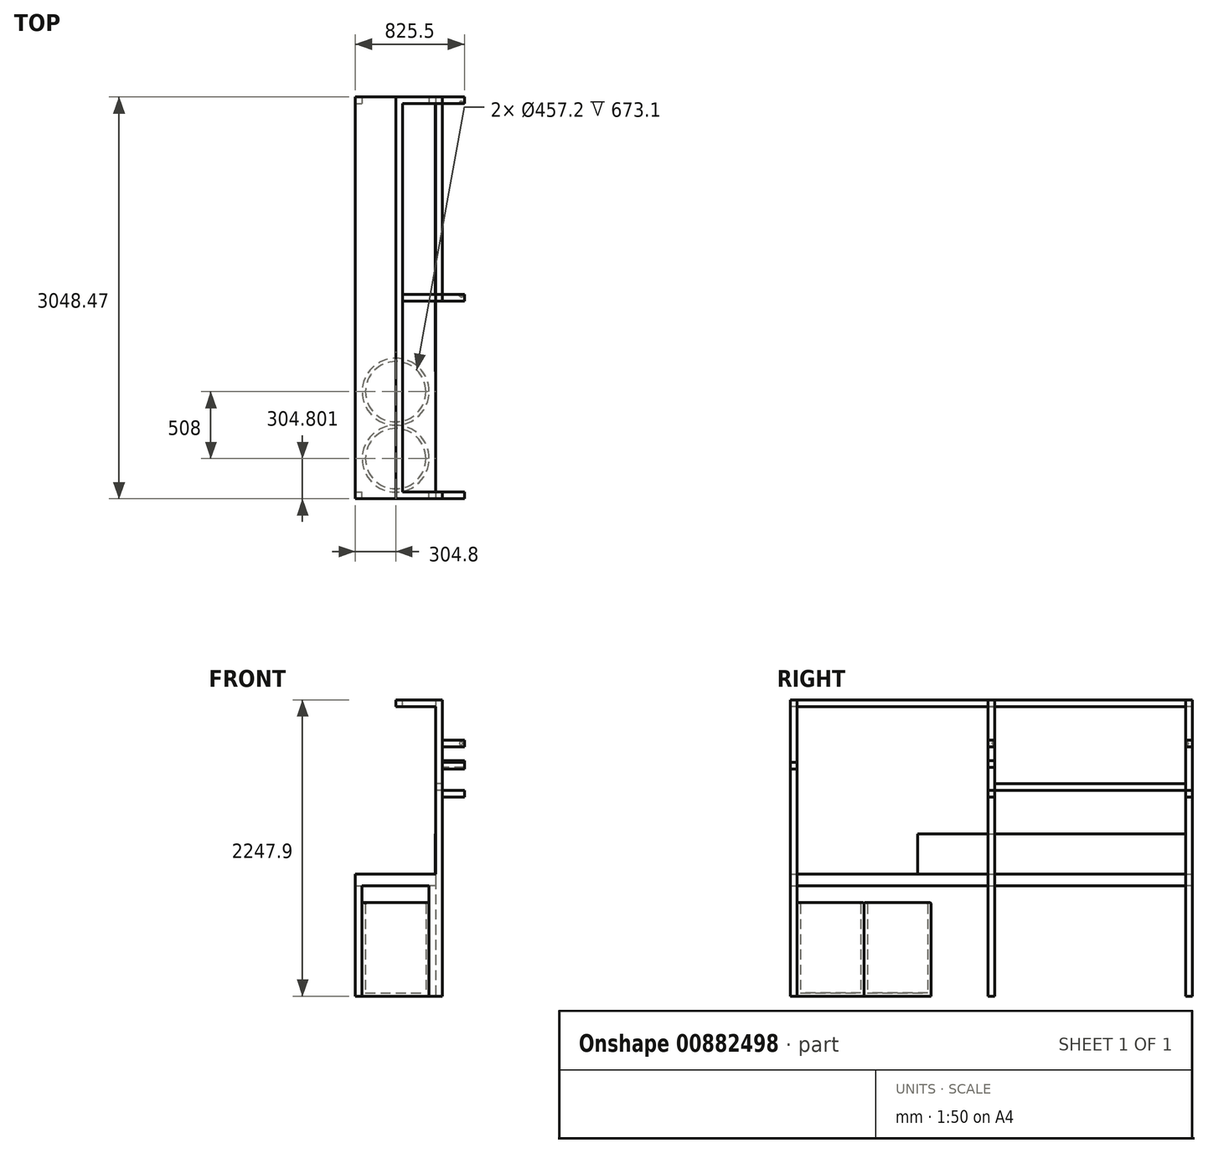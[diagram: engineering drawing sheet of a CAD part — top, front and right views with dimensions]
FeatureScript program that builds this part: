
annotation { "Feature Type Name" : "Feature", "Feature Type Description" : "" }
export const myFeature = defineFeature(function(context is Context, id is Id, definition is map)
    precondition{}
    {
        {
            var Q0;
            Q0=qCreatedBy(makeId("Right.planeOp"),FACE);
            var sketch = newSketch(context, id + "F0", { "sketchPlane" : qUnion([Q0])});
            skLineSegment(sketch, "E0.bottom", {"start": v(-1340.3, -28.95) * mm, "end": v(1707.7, -28.95) * mm});
            skLineSegment(sketch, "E0.top", {"start": v(-1340.3, -117.85) * mm, "end": v(1707.7, -117.85) * mm});
            skLineSegment(sketch, "E0.left", {"start": v(-1340.3, -28.95) * mm, "end": v(-1340.3, -117.85) * mm});
            skLineSegment(sketch, "E0.right", {"start": v(1707.7, -28.95) * mm, "end": v(1707.7, -117.85) * mm});
            skSolve(sketch);
        }
        {
            var Q0;
            Q0=makeQuery(id+"F0.imprint","IMPRINT",FACE,{"disambiguationData":[TD([[makeQuery(id+"F0.imprint","IMPRINT",EDGE,{"derivedFrom":sQuery(id+"F0.wireOp",EDGE,"E0.bottom")}),-1.0]])]});
            extrude(context, id + "F1", {"entities" : qUnion([Q0]), "oppositeDirection" : true, "depth" : 609.6 * mm, "offsetDistance" : 25.4 * mm});
        }
        {
            var Q0;
            Q0=makeQuery(id+"F1.opExtrude","SWEPT_FACE",FACE,{"disambiguationData":[OSD([sQuery(id+"F0.wireOp",EDGE,"E0.top")])]});
            var sketch = newSketch(context, id + "F2", { "sketchPlane" : qUnion([Q0])});
            skLineSegment(sketch, "E1.bottom", {"start": v(-609.6, 1340.3) * mm, "end": v(-558.8, 1340.3) * mm});
            skLineSegment(sketch, "E1.top", {"start": v(-609.6, 1289.5) * mm, "end": v(-558.8, 1289.5) * mm});
            skLineSegment(sketch, "E1.left", {"start": v(-609.6, 1340.3) * mm, "end": v(-609.6, 1289.5) * mm});
            skLineSegment(sketch, "E1.right", {"start": v(-558.8, 1340.3) * mm, "end": v(-558.8, 1289.5) * mm});
            skLineSegment(sketch, "E2.bottom", {"start": v(0, 1340.3) * mm, "end": v(-50.8, 1340.3) * mm});
            skLineSegment(sketch, "E2.top", {"start": v(0, 1289.5) * mm, "end": v(-50.8, 1289.5) * mm});
            skLineSegment(sketch, "E2.left", {"start": v(0, 1340.3) * mm, "end": v(0, 1289.5) * mm});
            skLineSegment(sketch, "E2.right", {"start": v(-50.8, 1340.3) * mm, "end": v(-50.8, 1289.5) * mm});
            skLineSegment(sketch, "E3.bottom", {"start": v(0, -1707.7) * mm, "end": v(-50.8, -1707.7) * mm});
            skLineSegment(sketch, "E3.top", {"start": v(0, -1656.9) * mm, "end": v(-50.8, -1656.9) * mm});
            skLineSegment(sketch, "E3.left", {"start": v(0, -1707.7) * mm, "end": v(0, -1656.9) * mm});
            skLineSegment(sketch, "E3.right", {"start": v(-50.8, -1707.7) * mm, "end": v(-50.8, -1656.9) * mm});
            skLineSegment(sketch, "E4.bottom", {"start": v(-609.6, -1707.7) * mm, "end": v(-558.8, -1707.7) * mm});
            skLineSegment(sketch, "E4.top", {"start": v(-609.6, -1656.9) * mm, "end": v(-558.8, -1656.9) * mm});
            skLineSegment(sketch, "E4.left", {"start": v(-609.6, -1707.7) * mm, "end": v(-609.6, -1656.9) * mm});
            skLineSegment(sketch, "E4.right", {"start": v(-558.8, -1707.7) * mm, "end": v(-558.8, -1656.9) * mm});
            skSolve(sketch);
        }
        {
            var Q0;
            Q0=qSketchRegion(id+"F2",true);
            extrude(context, id + "F3", {"entities" : qUnion([Q0]), "operationType" : NewBodyOperationType.ADD, "depth" : 838.2 * mm, "offsetDistance" : 25.4 * mm});
        }
        {
            var Q0;
            Q0=makeQuery(id+"F3.opExtrude","CAP_FACE",FACE,{"disambiguationData":[OSD([sQuery(id+"F2.wireOp",EDGE,"E4.bottom"),sQuery(id+"F2.wireOp",EDGE,"E4.top"),sQuery(id+"F2.wireOp",EDGE,"E4.left"),sQuery(id+"F2.wireOp",EDGE,"E4.right")])],"isStart":false});
            var sketch = newSketch(context, id + "F4", { "sketchPlane" : qUnion([Q0])});
            skCircle(sketch, "E5", {"center": v(-304.8, 1035.5) * mm, "radius": 254 * mm});
            skCircle(sketch, "E6", {"center": v(-304.8, 527.5) * mm, "radius": 254 * mm});
            skSolve(sketch);
        }
        {
            var Q0;
            Q0=qSketchRegion(id+"F4",true);
            extrude(context, id + "F5", {"entities" : qUnion([Q0]), "oppositeDirection" : true, "depth" : 711.2 * mm, "offsetDistance" : 25.4 * mm});
        }
        {
            var Q0;
            Q0=makeQuery(id+"F3.opExtrude","CAP_FACE",FACE,{"disambiguationData":[OSD([sQuery(id+"F2.wireOp",EDGE,"E2.bottom"),sQuery(id+"F2.wireOp",EDGE,"E2.top"),sQuery(id+"F2.wireOp",EDGE,"E2.left"),sQuery(id+"F2.wireOp",EDGE,"E2.right")])],"isStart":false});
            var sketch = newSketch(context, id + "F6", { "sketchPlane" : qUnion([Q0])});
            skLineSegment(sketch, "E7.bottom", {"start": v(0, 1340.3) * mm, "end": v(50.8, 1340.3) * mm});
            skLineSegment(sketch, "E7.top", {"start": v(0, 1289.5) * mm, "end": v(50.8, 1289.5) * mm});
            skLineSegment(sketch, "E7.left", {"start": v(0, 1340.3) * mm, "end": v(0, 1289.5) * mm});
            skLineSegment(sketch, "E7.right", {"start": v(50.8, 1340.3) * mm, "end": v(50.8, 1289.5) * mm});
            skLineSegment(sketch, "E8.bottom", {"start": v(0, -1656.9) * mm, "end": v(50.8, -1656.9) * mm});
            skLineSegment(sketch, "E8.top", {"start": v(0, -1707.7) * mm, "end": v(50.8, -1707.7) * mm});
            skLineSegment(sketch, "E8.left", {"start": v(0, -1656.9) * mm, "end": v(0, -1707.7) * mm});
            skLineSegment(sketch, "E8.right", {"start": v(50.8, -1656.9) * mm, "end": v(50.8, -1707.7) * mm});
            skSolve(sketch);
        }
        {
            var Q0;
            Q0=qSketchRegion(id+"F6",true);
            extrude(context, id + "F7", {"entities" : qUnion([Q0]), "operationType" : NewBodyOperationType.ADD, "oppositeDirection" : true, "depth" : 2247.9 * mm, "offsetDistance" : 25.4 * mm});
        }
        {
            var Q0;
            Q0=makeQuery(id+"F7.opExtrude","SWEPT_FACE",FACE,{"disambiguationData":[OSD([sQuery(id+"F6.wireOp",EDGE,"E8.left")])]});
            var sketch = newSketch(context, id + "F8", { "sketchPlane" : qUnion([Q0])});
            skLineSegment(sketch, "E9.bottom", {"start": v(-1707.7, 1291.85) * mm, "end": v(1340.3, 1291.85) * mm});
            skLineSegment(sketch, "E9.top", {"start": v(-1707.7, 1241.05) * mm, "end": v(1340.3, 1241.05) * mm});
            skLineSegment(sketch, "E9.left", {"start": v(-1707.7, 1291.85) * mm, "end": v(-1707.7, 1241.05) * mm});
            skLineSegment(sketch, "E9.right", {"start": v(1340.3, 1291.85) * mm, "end": v(1340.3, 1241.05) * mm});
            skSolve(sketch);
        }
        {
            var Q0;
            Q0=qSketchRegion(id+"F8",true);
            extrude(context, id + "F9", {"entities" : qUnion([Q0]), "operationType" : NewBodyOperationType.ADD, "depth" : 304.8 * mm, "offsetDistance" : 25.4 * mm});
        }
        {
            var Q0;
            Q0=makeQuery(id+"F9.boolean.opBoolean","MERGE",FACE,{"derivedFrom":[makeQuery(id+"F7.opExtrude","CAP_FACE",FACE,{"disambiguationData":[OSD([sQuery(id+"F6.wireOp",EDGE,"E7.bottom"),sQuery(id+"F6.wireOp",EDGE,"E7.top"),sQuery(id+"F6.wireOp",EDGE,"E7.left"),sQuery(id+"F6.wireOp",EDGE,"E7.right")])],"isStart":false}),makeQuery(id+"F7.opExtrude","CAP_FACE",FACE,{"disambiguationData":[OSD([sQuery(id+"F6.wireOp",EDGE,"E8.bottom"),sQuery(id+"F6.wireOp",EDGE,"E8.top"),sQuery(id+"F6.wireOp",EDGE,"E8.left"),sQuery(id+"F6.wireOp",EDGE,"E8.right")])],"isStart":false}),makeQuery(id+"F9.opExtrude","SWEPT_FACE",FACE,{"disambiguationData":[OSD([sQuery(id+"F8.wireOp",EDGE,"E9.bottom")])]})]});
            var sketch = newSketch(context, id + "F10", { "sketchPlane" : qUnion([Q0])});
            skLineSegment(sketch, "E10.bottom", {"start": v(0, 1656.9) * mm, "end": v(-254, 1656.9) * mm});
            skLineSegment(sketch, "E10.top", {"start": v(0, -1289.5) * mm, "end": v(-254, -1289.5) * mm});
            skLineSegment(sketch, "E10.left", {"start": v(0, 1656.9) * mm, "end": v(0, -1289.5) * mm});
            skLineSegment(sketch, "E10.right", {"start": v(-254, 1656.9) * mm, "end": v(-254, -1289.5) * mm});
            skSolve(sketch);
        }
        {
            var Q0;
            Q0=qSketchRegion(id+"F10",true);
            extrude(context, id + "F11", {"entities" : qUnion([Q0]), "operationType" : NewBodyOperationType.REMOVE, "endBound" : BoundingType.UP_TO_NEXT, "oppositeDirection" : true, "depth" : 25.4 * mm, "offsetDistance" : 25.4 * mm});
        }
        {
            var Q0;
            Q0=makeQuery(id+"F1.opExtrude","SWEPT_FACE",FACE,{"disambiguationData":[OSD([sQuery(id+"F0.wireOp",EDGE,"E0.bottom")])]});
            var sketch = newSketch(context, id + "F12", { "sketchPlane" : qUnion([Q0])});
            skLineSegment(sketch, "E11.bottom", {"start": v(0, 1656.9) * mm, "end": v(-3.17, 1656.9) * mm});
            skLineSegment(sketch, "E11.top", {"start": v(0, -375.1) * mm, "end": v(-3.17, -375.1) * mm});
            skLineSegment(sketch, "E11.left", {"start": v(0, 1656.9) * mm, "end": v(0, -375.1) * mm});
            skLineSegment(sketch, "E11.right", {"start": v(-3.18, 1656.9) * mm, "end": v(-3.17, -375.1) * mm});
            skSolve(sketch);
        }
        {
            var Q0;
            Q0=qSketchRegion(id+"F12",true);
            extrude(context, id + "F13", {"entities" : qUnion([Q0]), "depth" : 304.8 * mm, "offsetDistance" : 25.4 * mm});
        }
        {
            var Q0;
            Q0=makeQuery(id+"F7.boolean.opBoolean","MERGE",FACE,{"derivedFrom":[makeQuery(id+"F3.opExtrude","CAP_FACE",FACE,{"disambiguationData":[OSD([sQuery(id+"F2.wireOp",EDGE,"E2.bottom"),sQuery(id+"F2.wireOp",EDGE,"E2.top"),sQuery(id+"F2.wireOp",EDGE,"E2.left"),sQuery(id+"F2.wireOp",EDGE,"E2.right")])],"isStart":false}),makeQuery(id+"F7.opExtrude","CAP_FACE",FACE,{"disambiguationData":[OSD([sQuery(id+"F6.wireOp",EDGE,"E7.bottom"),sQuery(id+"F6.wireOp",EDGE,"E7.top"),sQuery(id+"F6.wireOp",EDGE,"E7.left"),sQuery(id+"F6.wireOp",EDGE,"E7.right")])],"isStart":true})]});
            var sketch = newSketch(context, id + "F14", { "sketchPlane" : qUnion([Q0])});
            skLineSegment(sketch, "E12.bottom", {"start": v(0, -158.3) * mm, "end": v(50.8, -158.3) * mm});
            skLineSegment(sketch, "E12.top", {"start": v(0, -209.1) * mm, "end": v(50.8, -209.1) * mm});
            skLineSegment(sketch, "E12.left", {"start": v(0, -158.3) * mm, "end": v(0, -209.1) * mm});
            skLineSegment(sketch, "E12.right", {"start": v(50.8, -158.3) * mm, "end": v(50.8, -209.1) * mm});
            skSolve(sketch);
        }
        {
            var Q0;
            Q0=qSketchRegion(id+"F14",true);
            extrude(context, id + "F15", {"entities" : qUnion([Q0]), "oppositeDirection" : true, "depth" : 2247.9 * mm, "offsetDistance" : 25.4 * mm});
        }
        {
            var Q0;
            Q0=makeQuery(id+"F5.opExtrude","CAP_FACE",FACE,{"disambiguationData":[OSD([sQuery(id+"F4.wireOp",EDGE,"E6")])],"isStart":false});
            shell(context, id + "F16", {"entities" : qUnion([Q0]), "thickness" : 25.4 * mm});
        }
        {
            var Q0;
            Q0=makeQuery(id+"F5.opExtrude","CAP_FACE",FACE,{"disambiguationData":[OSD([sQuery(id+"F4.wireOp",EDGE,"E5")])],"isStart":false});
            shell(context, id + "F17", {"entities" : qUnion([Q0]), "thickness" : 25.4 * mm});
        }
        {
            var Q0;
            Q0=makeQuery(id+"F5.opExtrude","CAP_FACE",FACE,{"disambiguationData":[OSD([sQuery(id+"F4.wireOp",EDGE,"E5")])],"isStart":false});
            fillet(context, id + "F18", {"entities" : qUnion([Q0]), "radius" : 12.7 * mm, "tangentPropagation" : true, "allowEdgeOverflow" : false});
        }
        {
            var Q0;
            Q0=makeQuery(id+"F5.opExtrude","CAP_FACE",FACE,{"disambiguationData":[OSD([sQuery(id+"F4.wireOp",EDGE,"E6")])],"isStart":false});
            fillet(context, id + "F19", {"entities" : qUnion([Q0]), "radius" : 12.7 * mm, "tangentPropagation" : true, "allowEdgeOverflow" : false});
        }
        {
            var Q0;
            Q0=makeQuery(id+"F11.boolean.opBoolean","MERGE",FACE,{"derivedFrom":[makeQuery(id+"F7.boolean.opBoolean","MERGE",FACE,{"derivedFrom":[makeQuery(id+"F3.opExtrude","SWEPT_FACE",FACE,{"disambiguationData":[OSD([sQuery(id+"F2.wireOp",EDGE,"E3.top")])]}),makeQuery(id+"F7.opExtrude","SWEPT_FACE",FACE,{"disambiguationData":[OSD([sQuery(id+"F6.wireOp",EDGE,"E8.bottom")])]})]})],"fromTools":[makeQuery(id+"F11.opExtrude","SWEPT_FACE",FACE,{"disambiguationData":[OSD([sQuery(id+"F10.wireOp",EDGE,"E10.bottom")])]})]});
            var sketch = newSketch(context, id + "F20", { "sketchPlane" : qUnion([Q0])});
            skLineSegment(sketch, "E13.bottom", {"start": v(0, 656.85) * mm, "end": v(50.8, 656.85) * mm});
            skLineSegment(sketch, "E13.top", {"start": v(0, 606.05) * mm, "end": v(50.8, 606.05) * mm});
            skLineSegment(sketch, "E13.left", {"start": v(0, 656.85) * mm, "end": v(0, 606.05) * mm});
            skLineSegment(sketch, "E13.right", {"start": v(50.8, 656.85) * mm, "end": v(50.8, 606.05) * mm});
            skSolve(sketch);
        }
        {
            var Q0;
            Q0=qSketchRegion(id+"F20",true);
            extrude(context, id + "F21", {"entities" : qUnion([Q0]), "endBound" : BoundingType.UP_TO_NEXT, "depth" : 25.4 * mm, "offsetDistance" : 25.4 * mm});
        }
        {
            var Q0;
            Q0=makeQuery(id+"F15.opExtrude","SWEPT_FACE",FACE,{"disambiguationData":[OSD([sQuery(id+"F14.wireOp",EDGE,"E12.right")])]});
            var sketch = newSketch(context, id + "F22", { "sketchPlane" : qUnion([Q0])});
            skLineSegment(sketch, "E14.bottom", {"start": v(158.3, 831.1) * mm, "end": v(209.1, 831.1) * mm});
            skLineSegment(sketch, "E14.top", {"start": v(158.3, 780.3) * mm, "end": v(209.1, 780.3) * mm});
            skLineSegment(sketch, "E14.left", {"start": v(158.3, 831.1) * mm, "end": v(158.3, 780.3) * mm});
            skLineSegment(sketch, "E14.right", {"start": v(209.1, 831.1) * mm, "end": v(209.1, 780.3) * mm});
            skLineSegment(sketch, "E15.bottom", {"start": v(-1340.3, 818.75) * mm, "end": v(-1289.5, 818.75) * mm});
            skLineSegment(sketch, "E15.top", {"start": v(-1340.3, 767.95) * mm, "end": v(-1289.5, 767.95) * mm});
            skLineSegment(sketch, "E15.left", {"start": v(-1340.3, 818.75) * mm, "end": v(-1340.3, 767.95) * mm});
            skLineSegment(sketch, "E15.right", {"start": v(-1289.5, 818.75) * mm, "end": v(-1289.5, 767.95) * mm});
            skSolve(sketch);
        }
        {
            var Q0;
            Q0=qSketchRegion(id+"F22",true);
            extrude(context, id + "F23", {"entities" : qUnion([Q0]), "depth" : 165.1 * mm, "offsetDistance" : 25.4 * mm});
        }
        {
            var Q0;
            Q0=makeQuery(id+"F15.opExtrude","SWEPT_FACE",FACE,{"disambiguationData":[OSD([sQuery(id+"F14.wireOp",EDGE,"E12.left")])]});
            var sketch = newSketch(context, id + "F24", { "sketchPlane" : qUnion([Q0])});
            skLineSegment(sketch, "E16.bottom", {"start": v(-209.1, 1291.85) * mm, "end": v(-158.3, 1291.85) * mm});
            skLineSegment(sketch, "E16.top", {"start": v(-209.1, 1241.05) * mm, "end": v(-158.3, 1241.05) * mm});
            skLineSegment(sketch, "E16.left", {"start": v(-209.1, 1291.85) * mm, "end": v(-209.1, 1241.05) * mm});
            skLineSegment(sketch, "E16.right", {"start": v(-158.3, 1291.85) * mm, "end": v(-158.3, 1241.05) * mm});
            skSolve(sketch);
        }
        {
            var Q0;
            Q0=qSketchRegion(id+"F24",true);
            extrude(context, id + "F25", {"entities" : qUnion([Q0]), "endBound" : BoundingType.UP_TO_NEXT, "depth" : 25.4 * mm, "offsetDistance" : 25.4 * mm});
        }
        {
            var Q0;
            Q0=makeQuery(id+"F15.opExtrude","SWEPT_FACE",FACE,{"disambiguationData":[OSD([sQuery(id+"F14.wireOp",EDGE,"E12.right")])]});
            var sketch = newSketch(context, id + "F26", { "sketchPlane" : qUnion([Q0])});
            skLineSegment(sketch, "E17.bottom", {"start": v(209.1, 606.05) * mm, "end": v(158.3, 606.05) * mm});
            skLineSegment(sketch, "E17.top", {"start": v(209.1, 555.25) * mm, "end": v(158.3, 555.25) * mm});
            skLineSegment(sketch, "E17.left", {"start": v(209.1, 606.05) * mm, "end": v(209.1, 555.25) * mm});
            skLineSegment(sketch, "E17.right", {"start": v(158.3, 606.05) * mm, "end": v(158.3, 555.25) * mm});
            skLineSegment(sketch, "E18.bottom", {"start": v(1657.36, 606.05) * mm, "end": v(1708.16, 606.05) * mm});
            skLineSegment(sketch, "E18.top", {"start": v(1657.36, 555.25) * mm, "end": v(1708.16, 555.25) * mm});
            skLineSegment(sketch, "E18.left", {"start": v(1657.36, 606.05) * mm, "end": v(1657.36, 555.25) * mm});
            skLineSegment(sketch, "E18.right", {"start": v(1708.16, 606.05) * mm, "end": v(1708.16, 555.25) * mm});
            skSolve(sketch);
        }
        {
            var Q0;
            Q0 = qSketchRegion(id + "F26", true);
            extrude(context, id + "F27", {"entities" : qUnion([Q0]), "depth" : 165.1 * mm, "offsetDistance" : 25.4 * mm});
        }
        {
            var Q0;
            Q0=makeQuery(id+"F15.opExtrude","SWEPT_FACE",FACE,{"disambiguationData":[OSD([sQuery(id+"F14.wireOp",EDGE,"E12.right")])]});
            var sketch = newSketch(context, id + "F28", { "sketchPlane" : qUnion([Q0])});
            skLineSegment(sketch, "E19.bottom", {"start": v(158.3, 987.05) * mm, "end": v(209.1, 987.05) * mm});
            skLineSegment(sketch, "E19.top", {"start": v(158.3, 936.25) * mm, "end": v(209.1, 936.25) * mm});
            skLineSegment(sketch, "E19.left", {"start": v(158.3, 987.05) * mm, "end": v(158.3, 936.25) * mm});
            skLineSegment(sketch, "E19.right", {"start": v(209.1, 987.05) * mm, "end": v(209.1, 936.25) * mm});
            skLineSegment(sketch, "E20.bottom", {"start": v(1656.9, 987.05) * mm, "end": v(1707.7, 987.05) * mm});
            skLineSegment(sketch, "E20.top", {"start": v(1656.9, 936.25) * mm, "end": v(1707.7, 936.25) * mm});
            skLineSegment(sketch, "E20.left", {"start": v(1656.9, 987.05) * mm, "end": v(1656.9, 936.25) * mm});
            skLineSegment(sketch, "E20.right", {"start": v(1707.7, 987.05) * mm, "end": v(1707.7, 936.25) * mm});
            skSolve(sketch);
        }
        {
            var Q0;
            Q0 = qSketchRegion(id + "F28", true);
            extrude(context, id + "F29", {"entities" : qUnion([Q0]), "depth" : 165.1 * mm, "offsetDistance" : 25.4 * mm});
        }
        {
            var Q0;
            Q0=makeQuery(id+"F29.opExtrude","SWEPT_FACE",FACE,{"disambiguationData":[OSD([sQuery(id+"F28.wireOp",EDGE,"E20.left")])]});
            var sketch = newSketch(context, id + "F30", { "sketchPlane" : qUnion([Q0])});
            skPoint(sketch, "E21", {"position": v(190.5, 961.65) * mm});
            skSolve(sketch);
        }
        {
            var Q0;
            Q0=sQuery(id+"F30.wireOp",VERTEX,"E21");
            var Q1;
            Q1=makeQuery(id+"F29.opExtrude","SWEPT_BODY",BODY,{"disambiguationData":[OSD([sQuery(id+"F28.wireOp",EDGE,"E20.bottom"),sQuery(id+"F28.wireOp",EDGE,"E20.top"),sQuery(id+"F28.wireOp",EDGE,"E20.left"),sQuery(id+"F28.wireOp",EDGE,"E20.right")])]});
            hole(context, id + "F31", {"style" : HoleStyle.SIMPLE, "endStyle" : HoleEndStyle.BLIND, "holeDiameter" : 25.4 * mm, "majorDiameter" : 6.35 * mm, "holeDepth" : 12.7 * mm, "isTappedThrough" : true, "tappedDepth" : 12.7 * mm, "tapClearance" : 3, "locations" : qUnion([Q0]), "scope" : qUnion([Q1])});
        }
        {
            var Q0;
            Q0=makeQuery(id+"F29.opExtrude","SWEPT_FACE",FACE,{"disambiguationData":[OSD([sQuery(id+"F28.wireOp",EDGE,"E19.right")])]});
            var sketch = newSketch(context, id + "F32", { "sketchPlane" : qUnion([Q0])});
            skPoint(sketch, "E22", {"position": v(-190.5, 961.65) * mm});
            skSolve(sketch);
        }
        {
            var Q0;
            Q0=sQuery(id+"F32.wireOp",VERTEX,"E22");
            var Q1;
            Q1=makeQuery(id+"F29.opExtrude","SWEPT_BODY",BODY,{"disambiguationData":[OSD([sQuery(id+"F28.wireOp",EDGE,"E19.bottom"),sQuery(id+"F28.wireOp",EDGE,"E19.top"),sQuery(id+"F28.wireOp",EDGE,"E19.left"),sQuery(id+"F28.wireOp",EDGE,"E19.right")])]});
            hole(context, id + "F33", {"style" : HoleStyle.SIMPLE, "endStyle" : HoleEndStyle.BLIND, "holeDiameter" : 25.4 * mm, "majorDiameter" : 6.35 * mm, "holeDepth" : 12.7 * mm, "isTappedThrough" : true, "tappedDepth" : 12.7 * mm, "tapClearance" : 3, "locations" : qUnion([Q0]), "scope" : qUnion([Q1])});
        }
    });
